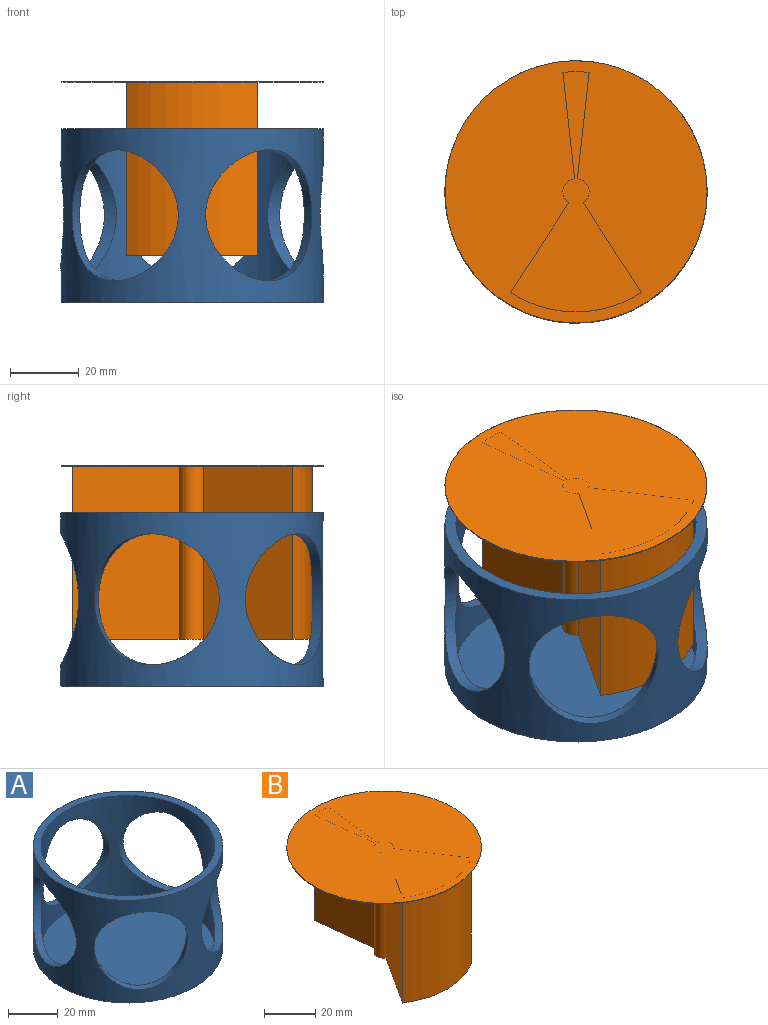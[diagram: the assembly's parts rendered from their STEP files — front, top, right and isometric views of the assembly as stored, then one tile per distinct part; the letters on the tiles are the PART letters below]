
ASSEMBLY  parts=2 mates=1
PART A: 10 faces, bbox 84.2x80.1x50.5 mm
  f0: cylinder r=38.1mm len=76.2mm, axis (0,0,-1), area 6201.7mm2, adj f2,f3,f5,f6,f7,f8,f9
  f1: cylinder r=34.92mm len=69.85mm, axis (0,0,1), area 5105.9mm2, adj f2,f4,f5,f6,f7,f8,f9
  f2: plane 76.2x76.2mm, normal (0,0,1), area 728.4mm2, adj f0,f1
  f3: plane 76.2x76.2mm, normal (0,0,-1), area 4560.4mm2, adj f0
  f4: plane 69.85x69.85mm, normal (0,0,1), area 3832mm2, adj f1
  f5: cylinder r=19.05mm len=38.1mm, axis (0,-1,0), area 411.1mm2, adj f0,f1
  f6: cylinder r=19.05mm len=38.96mm, axis (0.95,-0.31,0), area 410.8mm2, adj f0,f1
  f7: cylinder r=19.05mm len=38.1mm, axis (0.59,0.81,0), area 410.8mm2, adj f0,f1
  f8: cylinder r=19.05mm len=38.1mm, axis (-0.59,0.81,0), area 410.8mm2, adj f0,f1
  f9: cylinder r=19.05mm len=38.96mm, axis (-0.95,-0.31,0), area 410.7mm2, adj f0,f1
PART B: 12 faces, bbox 76.2x76.2x50.5 mm
  f0: cylinder r=38.1mm len=76.2mm, axis (0,0,-1), area 60.8mm2, adj f1,f2
  f1: plane 76.2x76.2mm, normal (0,0,1), area 4560.4mm2, adj f0
  f2: plane 76.2x76.2mm, normal (0,0,-1), area 3687.7mm2, adj f0,f3,f4,f5,f6,f7,f8,f9
  f3: cylinder r=34.92mm len=50.29mm, axis (0,0,1), area 2026.7mm2, adj f2,f4,f10,f11
  f4: plane 50.29x26.08mm, normal (-0.84,0.55,0), area 1564.8mm2, adj f2,f3,f5,f11
  f5: cylinder r=3.81mm len=50.29mm, axis (0,0,1), area 470.5mm2, adj f2,f4,f6,f11
  f6: plane 50.29x30.93mm, normal (-0.99,-0.11,0), area 1564.8mm2, adj f2,f5,f7,f11
  f7: cylinder r=34.92mm len=50.29mm, axis (0,0,1), area 384mm2, adj f2,f6,f8,f11
  f8: plane 50.29x30.93mm, normal (0.99,-0.11,0), area 1564.8mm2, adj f2,f7,f9,f11
  f9: cylinder r=3.81mm len=50.29mm, axis (0,0,1), area 470.5mm2, adj f2,f8,f10,f11
  f10: plane 50.29x26.08mm, normal (0.84,0.55,0), area 1564.8mm2, adj f2,f3,f9,f11
  f11: plane 69.85x38.1mm, normal (0,0,-1), area 872.7mm2, adj f3,f4,f5,f6,f7,f8,f9,f10
PLACE A t=(-104.06,20.94,82.47)mm
PLACE B t=(-104.06,20.94,146.54)mm
MATE cylindrical A.f1 <-> B.f0  axis (0,0,1) through (-104.06,20.94,82.72)mm
